# Revit family: Window_Commercial_Aluminum_CF-Right-Split-ROTO_3_H450_Quaker
name_source: partatom
category: Windows
units: mm (PartAtom-declared; Revit-internal decimal feet)

## family parameters
Always vertical = Yes
Classification Number = 23.30.20.00
Cut with Voids When Loaded = No
Host = Wall
Room Calculation Point = No
Shared = No

## types (1)
- Window_Commercial_Aluminum_CF-Right-Split-ROTO_3_H450_Quaker
    Analytic Construction = <None>
    Default Sill Height = 3' - 0"
    Define Thermal Properties by = Schematic Type
    Glass = Glass
    Handle = Handle_Alluminum
    Height = 5' - 0"
    Keynote = 08 51 13
    Manufacturer = Quaker Windows & Doors
    Product Page URL = https://www.arcat.com
    Rough Height = 0' - 0"
    Rough Width = 0' - 0"
    URL = https://www.quakercommercialwindows.com
    Wall Closure = By host
    Width = 5' - 0"
    Window Frame = Alluminum

## geometry (parser evidence)
native form markers: Sweep x15
no freeform markers — native parametric forms only
